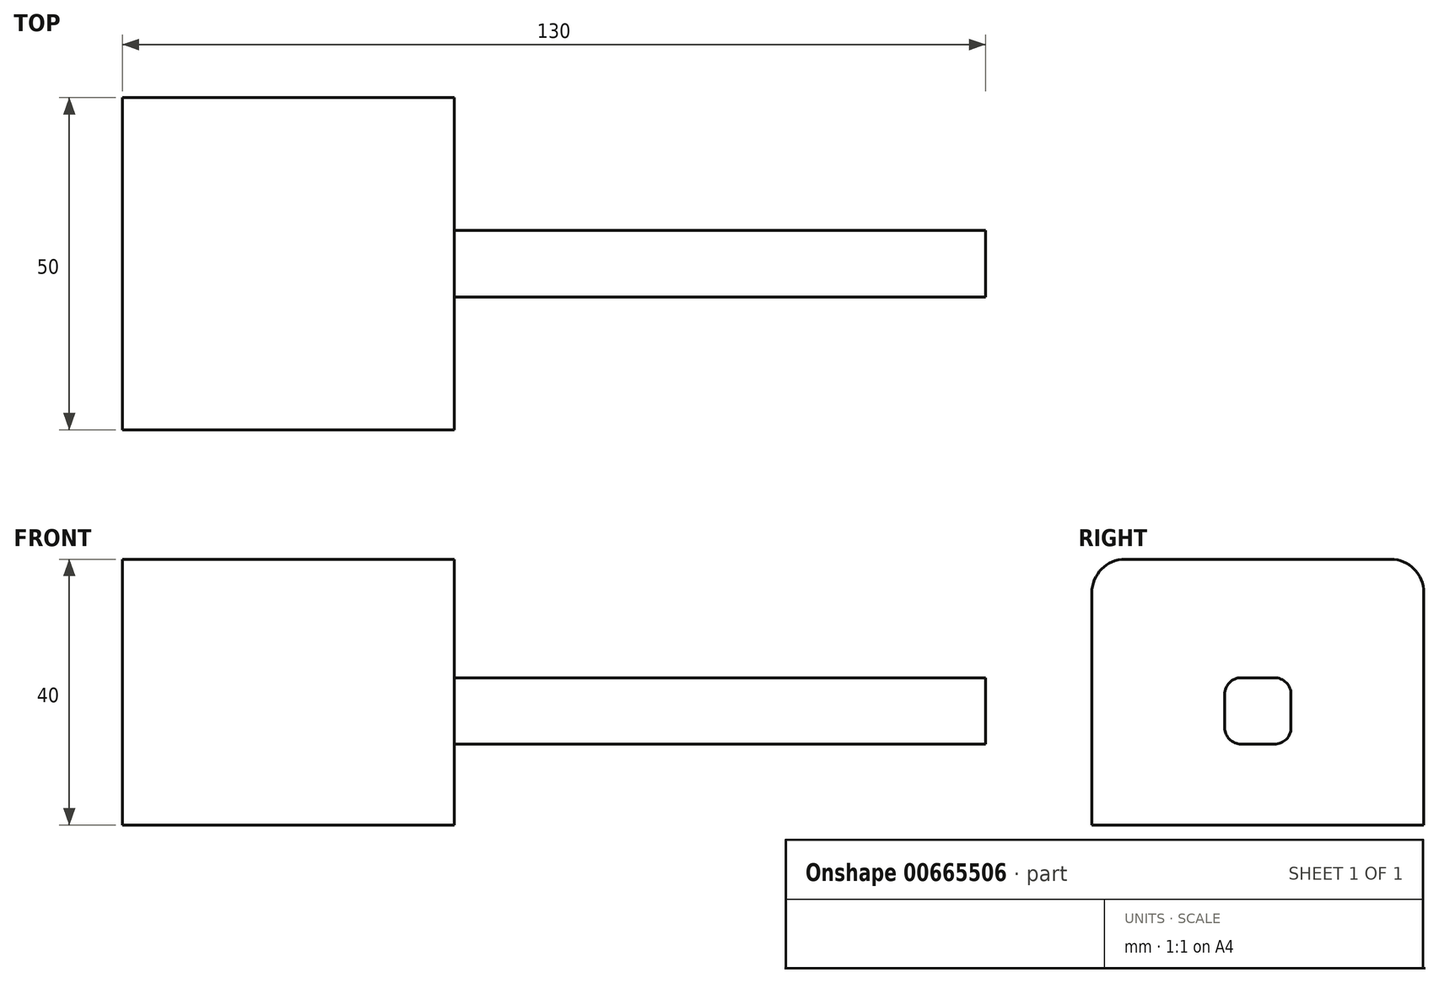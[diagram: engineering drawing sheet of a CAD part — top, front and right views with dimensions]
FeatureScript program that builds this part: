
annotation { "Feature Type Name" : "Feature", "Feature Type Description" : "" }
export const myFeature = defineFeature(function(context is Context, id is Id, definition is map)
    precondition{}
    {
        {
            var Q0;
            Q0=qCreatedBy(makeId("Top.planeOp"),FACE);
            var sketch = newSketch(context, id + "F0", { "sketchPlane" : qUnion([Q0])});
            skLineSegment(sketch, "E0.bottom", {"start": v(25, -25) * mm, "end": v(-25, -25) * mm});
            skLineSegment(sketch, "E0.top", {"start": v(25, 25) * mm, "end": v(-25, 25) * mm});
            skLineSegment(sketch, "E0.left", {"start": v(25, -25) * mm, "end": v(25, 25) * mm});
            skLineSegment(sketch, "E0.right", {"start": v(-25, -25) * mm, "end": v(-25, 25) * mm});
            skPoint(sketch, "E0.middle", {"position": v(0, 0) * mm});
            skSolve(sketch);
        }
        {
            var Q0;
            Q0=makeQuery(id+"F0.imprint","IMPRINT",FACE,{"disambiguationData":[TD([[makeQuery(id+"F0.imprint","IMPRINT",EDGE,{"derivedFrom":sQuery(id+"F0.wireOp",EDGE,"E0.bottom")}),-1.0]])]});
            extrude(context, id + "F1", {"entities" : qUnion([Q0]), "depth" : 40 * mm, "offsetDistance" : 25 * mm});
        }
        {
            var Q0;
            Q0=makeQuery(id+"F1.opExtrude","SWEPT_FACE",FACE,{"disambiguationData":[OSD([sQuery(id+"F0.wireOp",EDGE,"E0.left")])]});
            var sketch = newSketch(context, id + "F2", { "sketchPlane" : qUnion([Q0])});
            skLineSegment(sketch, "E1.bottom", {"start": v(5, 12.17) * mm, "end": v(-5, 12.17) * mm});
            skLineSegment(sketch, "E1.top", {"start": v(5, 22.17) * mm, "end": v(-5, 22.17) * mm});
            skLineSegment(sketch, "E1.left", {"start": v(5, 12.17) * mm, "end": v(5, 22.17) * mm});
            skLineSegment(sketch, "E1.right", {"start": v(-5, 12.17) * mm, "end": v(-5, 22.17) * mm});
            skPoint(sketch, "E1.middle", {"position": v(0, 17.17) * mm});
            skSolve(sketch);
        }
        {
            var Q0;
            Q0 = qSketchRegion(id + "F2", true);
            extrude(context, id + "F3", {"entities" : qUnion([Q0]), "operationType" : NewBodyOperationType.ADD, "depth" : 80 * mm, "offsetDistance" : 25 * mm});
        }
        {
            var Q0;
            Q0=makeQuery(id+"F3.opExtrude","SWEPT_EDGE",EDGE,{"disambiguationData":[OSD([sQuery(id+"F2.wireOp",EDGE,"E1.top"),sQuery(id+"F2.wireOp",EDGE,"E1.left")])]});
            fillet(context, id + "F4", {"entities" : qUnion([Q0]), "radius" : 2.5 * mm, "tangentPropagation" : true, "allowEdgeOverflow" : false});
        }
        {
            var Q0;
            Q0=makeQuery(id+"F3.opExtrude","SWEPT_EDGE",EDGE,{"disambiguationData":[OSD([sQuery(id+"F2.wireOp",EDGE,"E1.top"),sQuery(id+"F2.wireOp",EDGE,"E1.right")])]});
            fillet(context, id + "F5", {"entities" : qUnion([Q0]), "radius" : 2.5 * mm, "tangentPropagation" : true, "allowEdgeOverflow" : false});
        }
        {
            var Q0;
            Q0=makeQuery(id+"F3.opExtrude","SWEPT_EDGE",EDGE,{"disambiguationData":[OSD([sQuery(id+"F2.wireOp",EDGE,"E1.bottom"),sQuery(id+"F2.wireOp",EDGE,"E1.right")])]});
            fillet(context, id + "F6", {"entities" : qUnion([Q0]), "radius" : 2.5 * mm, "tangentPropagation" : true, "allowEdgeOverflow" : false});
        }
        {
            var Q0;
            Q0=makeQuery(id+"F3.opExtrude","SWEPT_EDGE",EDGE,{"disambiguationData":[OSD([sQuery(id+"F2.wireOp",EDGE,"E1.bottom"),sQuery(id+"F2.wireOp",EDGE,"E1.left")])]});
            fillet(context, id + "F7", {"entities" : qUnion([Q0]), "radius" : 2.5 * mm, "tangentPropagation" : true, "allowEdgeOverflow" : false});
        }
        {
            var Q0;
            Q0=makeQuery(id+"F1.opExtrude","CAP_EDGE",EDGE,{"disambiguationData":[OSD([sQuery(id+"F0.wireOp",EDGE,"E0.top")])],"isStart":false});
            fillet(context, id + "F8", {"entities" : qUnion([Q0]), "radius" : 5 * mm, "tangentPropagation" : true, "allowEdgeOverflow" : false});
        }
        {
            var Q0;
            Q0=makeQuery(id+"F1.opExtrude","CAP_EDGE",EDGE,{"disambiguationData":[OSD([sQuery(id+"F0.wireOp",EDGE,"E0.bottom")])],"isStart":false});
            fillet(context, id + "F9", {"entities" : qUnion([Q0]), "radius" : 5 * mm, "tangentPropagation" : true, "allowEdgeOverflow" : false});
        }
    });
